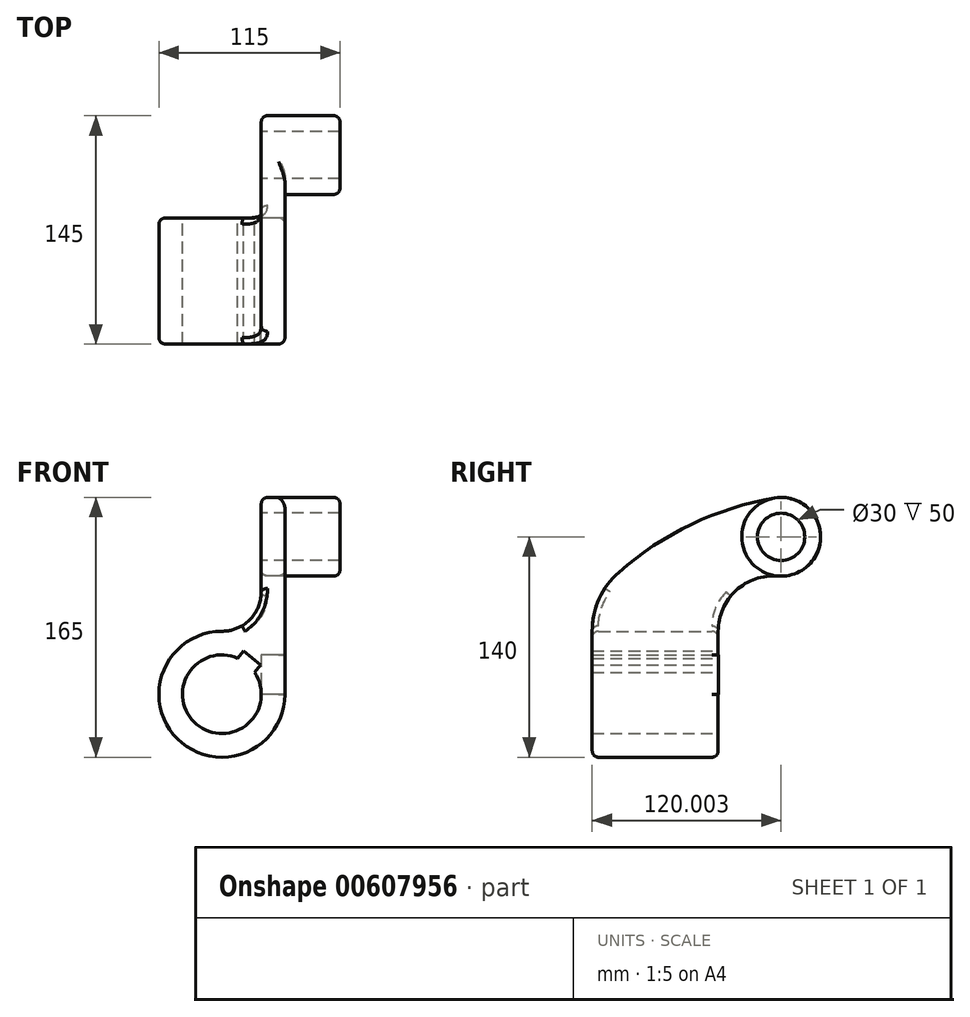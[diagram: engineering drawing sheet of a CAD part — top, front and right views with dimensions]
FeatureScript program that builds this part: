
annotation { "Feature Type Name" : "Feature", "Feature Type Description" : "" }
export const myFeature = defineFeature(function(context is Context, id is Id, definition is map)
    precondition{}
    {
        {
            var Q0;
            Q0=qCreatedBy(makeId("Right.planeOp"),FACE);
            var sketch = newSketch(context, id + "F0", { "sketchPlane" : qUnion([Q0])});
            skLineSegment(sketch, "E0", {"start": v(-111.3, 0) * mm, "end": v(0, 0) * mm, "construction": true});
            skLineSegment(sketch, "E1.bottom", {"start": v(-96.43, 25) * mm, "end": v(-16.43, 25) * mm});
            skLineSegment(sketch, "E1.top", {"start": v(-96.43, 40) * mm, "end": v(-16.43, 40) * mm});
            skLineSegment(sketch, "E1.left", {"start": v(-96.43, 25) * mm, "end": v(-96.43, 40) * mm});
            skLineSegment(sketch, "E1.right", {"start": v(-16.43, 25) * mm, "end": v(-16.43, 40) * mm});
            skCircle(sketch, "E2", {"center": v(23.57, 100) * mm, "radius": 15 * mm});
            skCircle(sketch, "E3", {"center": v(23.57, 100) * mm, "radius": 25 * mm});
            skArc(sketch, "E4", {"start": v(21.58, 75.08) * mm, "mid": v(-5.1, 65.86) * mm, "end": v(-16.43, 40) * mm});
            skArc(sketch, "E5", {"start": v(-79.48, 77.52) * mm, "mid": v(-92, 60.58) * mm, "end": v(-96.43, 40) * mm});
            skArc(sketch, "E6", {"start": v(19.4, 124.65) * mm, "mid": v(-33.33, 107.99) * mm, "end": v(-79.48, 77.52) * mm});
            skLineSegment(sketch, "E7.bottom", {"start": v(-16.34, 0) * mm, "end": v(-96.43, 0) * mm});
            skLineSegment(sketch, "E7.top", {"start": v(-16.34, 25) * mm, "end": v(-96.43, 25) * mm});
            skLineSegment(sketch, "E7.left", {"start": v(-16.34, 0) * mm, "end": v(-16.34, 25) * mm});
            skLineSegment(sketch, "E7.right", {"start": v(-96.43, 0) * mm, "end": v(-96.43, 25) * mm});
            skSolve(sketch);
        }
        {
            var Q0;
            Q0=makeQuery(id+"F0.imprint","IMPRINT",FACE,{"disambiguationData":[TD([[makeQuery(id+"F0.imprint","IMPRINT",EDGE,{"derivedFrom":sQuery(id+"F0.wireOp",EDGE,"E1.top")}),-1.0]])]});
            var Q1;
            Q1=sQuery(id+"F0.wireOp",EDGE,"E7.bottom");
            revolve(context, id + "F1", {"entities" : qUnion([Q0]), "axis" : qUnion([Q1]), "revolveType" : RevolveType.FULL});
        }
        {
            var Q0;
            Q0=makeQuery(id+"F0.imprint","IMPRINT",FACE,{"disambiguationData":[TD([[makeQuery(id+"F0.imprint","IMPRINT",EDGE,{"derivedFrom":sQuery(id+"F0.wireOp",EDGE,"E1.top")}),1.0]])]});
            var Q1;
            Q1=makeQuery(id+"F0.imprint","IMPRINT",FACE,{"disambiguationData":[TD([[makeQuery(id+"F0.imprint","IMPRINT",EDGE,{"derivedFrom":sQuery(id+"F0.wireOp",EDGE,"E7.bottom")}),-1.0]])]});
            var Q2;
            Q2=makeQuery(id+"F0.imprint","IMPRINT",FACE,{"disambiguationData":[TD([[makeQuery(id+"F0.imprint","IMPRINT",EDGE,{"derivedFrom":sQuery(id+"F0.wireOp",EDGE,"E1.top")}),-1.0]])]});
            extrude(context, id + "F2", {"entities" : qUnion([Q0, Q1, Q2]), "operationType" : NewBodyOperationType.ADD, "depth" : 40 * mm, "offsetDistance" : 25 * mm, "hasSecondDirection" : true, "secondDirectionOppositeDirection" : false, "secondDirectionDepth" : 25 * mm});
        }
        {
            var Q0;
            Q0=makeQuery(id+"F0.imprint","IMPRINT",FACE,{"disambiguationData":[TD([[makeQuery(id+"F0.imprint","IMPRINT",EDGE,{"derivedFrom":sQuery(id+"F0.wireOp",EDGE,"E2")}),-1.0]])]});
            extrude(context, id + "F3", {"entities" : qUnion([Q0]), "operationType" : NewBodyOperationType.ADD, "depth" : 75 * mm, "offsetDistance" : 25 * mm, "hasSecondDirection" : true, "secondDirectionOppositeDirection" : false, "secondDirectionDepth" : 25 * mm});
        }
        {
            var Q0;
            Q0=makeQuery(id+"F2.boolean.opBoolean","INTERSECT",EDGE,{"derivedFrom":[makeQuery(id+"F1.opRevolve","SWEPT_FACE",FACE,{"disambiguationData":[OSD([sQuery(id+"F0.wireOp",EDGE,"E1.top")])]}),makeQuery(id+"F2.opExtrude","CAP_FACE",FACE,{"disambiguationData":[OSD([sQuery(id+"F0.wireOp",EDGE,"E1.left"),sQuery(id+"F0.wireOp",EDGE,"E1.right"),sQuery(id+"F0.wireOp",EDGE,"E3"),sQuery(id+"F0.wireOp",EDGE,"E4"),sQuery(id+"F0.wireOp",EDGE,"E5"),sQuery(id+"F0.wireOp",EDGE,"E6"),sQuery(id+"F0.wireOp",EDGE,"E7.bottom"),sQuery(id+"F0.wireOp",EDGE,"E7.top"),sQuery(id+"F0.wireOp",EDGE,"E7.left"),sQuery(id+"F0.wireOp",EDGE,"E7.right")])],"isStart":true})]});
            var Q1;
            Q1=makeQuery(id+"F2.opExtrude","CAP_EDGE",EDGE,{"disambiguationData":[OSD([sQuery(id+"F0.wireOp",EDGE,"E3")])],"isStart":false});
            fillet(context, id + "F4", {"entities" : qUnion([Q0, Q1]), "radius" : 25 * mm, "tangentPropagation" : true, "allowEdgeOverflow" : false});
        }
        {
            var Q0;
            Q0=makeQuery(id+"F2.opExtrude","CAP_EDGE",EDGE,{"disambiguationData":[OSD([sQuery(id+"F0.wireOp",EDGE,"E6")])],"isStart":true});
            var Q1;
            Q1=makeQuery(id+"F3.opExtrude","CAP_EDGE",EDGE,{"disambiguationData":[OSD([sQuery(id+"F0.wireOp",EDGE,"E3")])],"isStart":false});
            var Q2;
            Q2=makeQuery(id+"F2.opExtrude","CAP_EDGE",EDGE,{"disambiguationData":[OSD([sQuery(id+"F0.wireOp",EDGE,"E4")])],"isStart":false});
            fillet(context, id + "F5", {"entities" : qUnion([Q0, Q1, Q2]), "radius" : 4 * mm, "tangentPropagation" : true, "allowEdgeOverflow" : false});
        }
        {
            var Q0;
            Q0=qCreatedBy(makeId("Front.planeOp"),FACE);
            var sketch = newSketch(context, id + "F6", { "sketchPlane" : qUnion([Q0])});
            skLineSegment(sketch, "E8.bottom", {"start": v(13.92, 27.48) * mm, "end": v(24.65, 18.48) * mm});
            skLineSegment(sketch, "E8.top", {"start": v(-5.36, 4.5) * mm, "end": v(5.36, -4.5) * mm});
            skLineSegment(sketch, "E8.left", {"start": v(13.92, 27.48) * mm, "end": v(-5.36, 4.5) * mm});
            skLineSegment(sketch, "E8.right", {"start": v(24.65, 18.48) * mm, "end": v(5.36, -4.5) * mm});
            skSolve(sketch);
        }
        {
            var Q0;
            Q0 = qSketchRegion(id + "F6", true);
            extrude(context, id + "F7", {"entities" : qUnion([Q0]), "operationType" : NewBodyOperationType.REMOVE, "endBound" : BoundingType.THROUGH_ALL, "depth" : 80 * mm, "offsetDistance" : 25 * mm});
        }
    });
